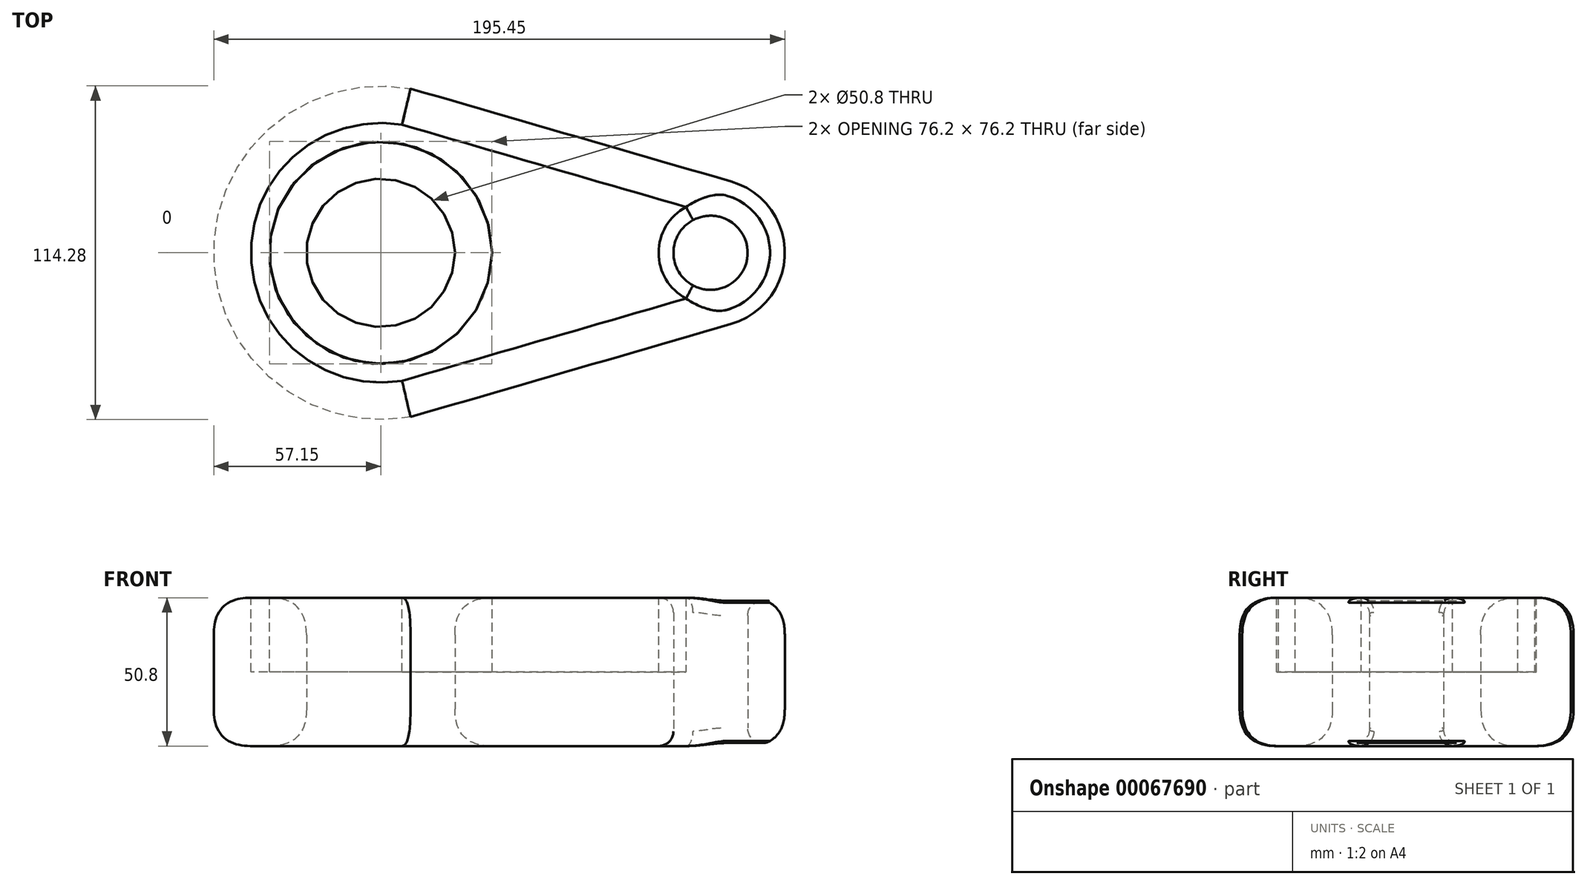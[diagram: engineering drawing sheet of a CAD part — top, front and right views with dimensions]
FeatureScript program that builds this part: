
annotation { "Feature Type Name" : "Feature", "Feature Type Description" : "" }
export const myFeature = defineFeature(function(context is Context, id is Id, definition is map)
    precondition{}
    {
        {
            var Q0;
            Q0=qCreatedBy(makeId("Top.planeOp"),FACE);
            var sketch = newSketch(context, id + "F0", { "sketchPlane" : qUnion([Q0])});
            skCircle(sketch, "E0", {"center": v(112.9, 0) * mm, "radius": 25.4 * mm});
            skCircle(sketch, "E1", {"center": v(0, 0) * mm, "radius": 25.4 * mm});
            skCircle(sketch, "E2", {"center": v(112.9, 0) * mm, "radius": 12.7 * mm});
            skCircle(sketch, "E3", {"center": v(0, 0) * mm, "radius": 57.15 * mm});
            skLineSegment(sketch, "E4", {"start": v(10.2, 56.23) * mm, "end": v(119.98, 24.4) * mm});
            skLineSegment(sketch, "E5", {"start": v(10.2, -56.23) * mm, "end": v(119.98, -24.4) * mm});
            skSolve(sketch);
        }
        {
            var Q0;
            {var subQ0=sQuery(id+"F0.wireOp",EDGE,"E4");var subQ1=sQuery(id+"F0.wireOp",EDGE,"E0");var subQ2=makeQuery(id+"F0.imprint","INTERSECT",VERTEX,{"derivedFrom":[subQ1,subQ0]});Q0=makeQuery(id+"F0.imprint","IMPRINT",FACE,{"disambiguationData":[TD([[makeQuery(id+"F0.imprint","IMPRINT",EDGE,{"disambiguationData":[TD([[subQ2,-1.0]])],"derivedFrom":subQ1}),-1.0]])]});}
            var Q1;
            Q1=makeQuery(id+"F0.imprint","IMPRINT",FACE,{"disambiguationData":[TD([[makeQuery(id+"F0.imprint","IMPRINT",EDGE,{"derivedFrom":sQuery(id+"F0.wireOp",EDGE,"E1")}),-1.0]])]});
            var Q2;
            Q2=makeQuery(id+"F0.imprint","IMPRINT",FACE,{"disambiguationData":[TD([[makeQuery(id+"F0.imprint","IMPRINT",EDGE,{"derivedFrom":sQuery(id+"F0.wireOp",EDGE,"E2")}),-1.0]])]});
            extrude(context, id + "F1", {"entities" : qUnion([Q0, Q1, Q2]), "depth" : 50.8 * mm});
        }
        {
            var Q0;
            Q0=makeQuery(id+"F1.opExtrude","CAP_EDGE",EDGE,{"disambiguationData":[OSD([sQuery(id+"F0.wireOp",EDGE,"E3")])],"isStart":false});
            var Q1;
            Q1=makeQuery(id+"F1.opExtrude","CAP_EDGE",EDGE,{"disambiguationData":[OSD([sQuery(id+"F0.wireOp",EDGE,"E5")])],"isStart":false});
            var Q2;
            Q2=makeQuery(id+"F1.opExtrude","CAP_EDGE",EDGE,{"disambiguationData":[OSD([sQuery(id+"F0.wireOp",EDGE,"E1")])],"isStart":true});
            var Q3;
            Q3=makeQuery(id+"F1.opExtrude","CAP_EDGE",EDGE,{"disambiguationData":[OSD([sQuery(id+"F0.wireOp",EDGE,"E1")])],"isStart":false});
            var Q4;
            Q4=makeQuery(id+"F1.opExtrude","CAP_EDGE",EDGE,{"disambiguationData":[OSD([sQuery(id+"F0.wireOp",EDGE,"E5")])],"isStart":true});
            var Q5;
            Q5=makeQuery(id+"F1.opExtrude","CAP_EDGE",EDGE,{"disambiguationData":[OSD([sQuery(id+"F0.wireOp",EDGE,"E3")])],"isStart":true});
            fillet(context, id + "F2", {"entities" : qUnion([Q0, Q1, Q2, Q3, Q4, Q5]), "radius" : 12.7 * mm, "tangentPropagation" : true, "rho" : 0.5, "crossSection" : FilletCrossSection.CONIC, "allowEdgeOverflow" : false});
        }
        {
            var Q0;
            Q0=makeQuery(id+"F1.opExtrude","CAP_EDGE",EDGE,{"disambiguationData":[OSD([sQuery(id+"F0.wireOp",EDGE,"E2")])],"isStart":false});
            var Q1;
            Q1=makeQuery(id+"F1.opExtrude","CAP_EDGE",EDGE,{"disambiguationData":[OSD([sQuery(id+"F0.wireOp",EDGE,"E2")])],"isStart":true});
            fillet(context, id + "F3", {"entities" : qUnion([Q0, Q1]), "radius" : 5.08 * mm, "tangentPropagation" : true, "allowEdgeOverflow" : false});
        }
        {
            var Q0;
            Q0=makeQuery(id+"F1.opExtrude","CAP_FACE",FACE,{"disambiguationData":[OSD([sQuery(id+"F0.wireOp",EDGE,"E0"),sQuery(id+"F0.wireOp",EDGE,"E1"),sQuery(id+"F0.wireOp",EDGE,"E2"),sQuery(id+"F0.wireOp",EDGE,"E3"),sQuery(id+"F0.wireOp",EDGE,"E4"),sQuery(id+"F0.wireOp",EDGE,"E5")])],"isStart":false});
            extrude(context, id + "F4", {"entities" : qUnion([Q0]), "operationType" : NewBodyOperationType.REMOVE, "oppositeDirection" : true, "depth" : 25.4 * mm});
        }
    });
